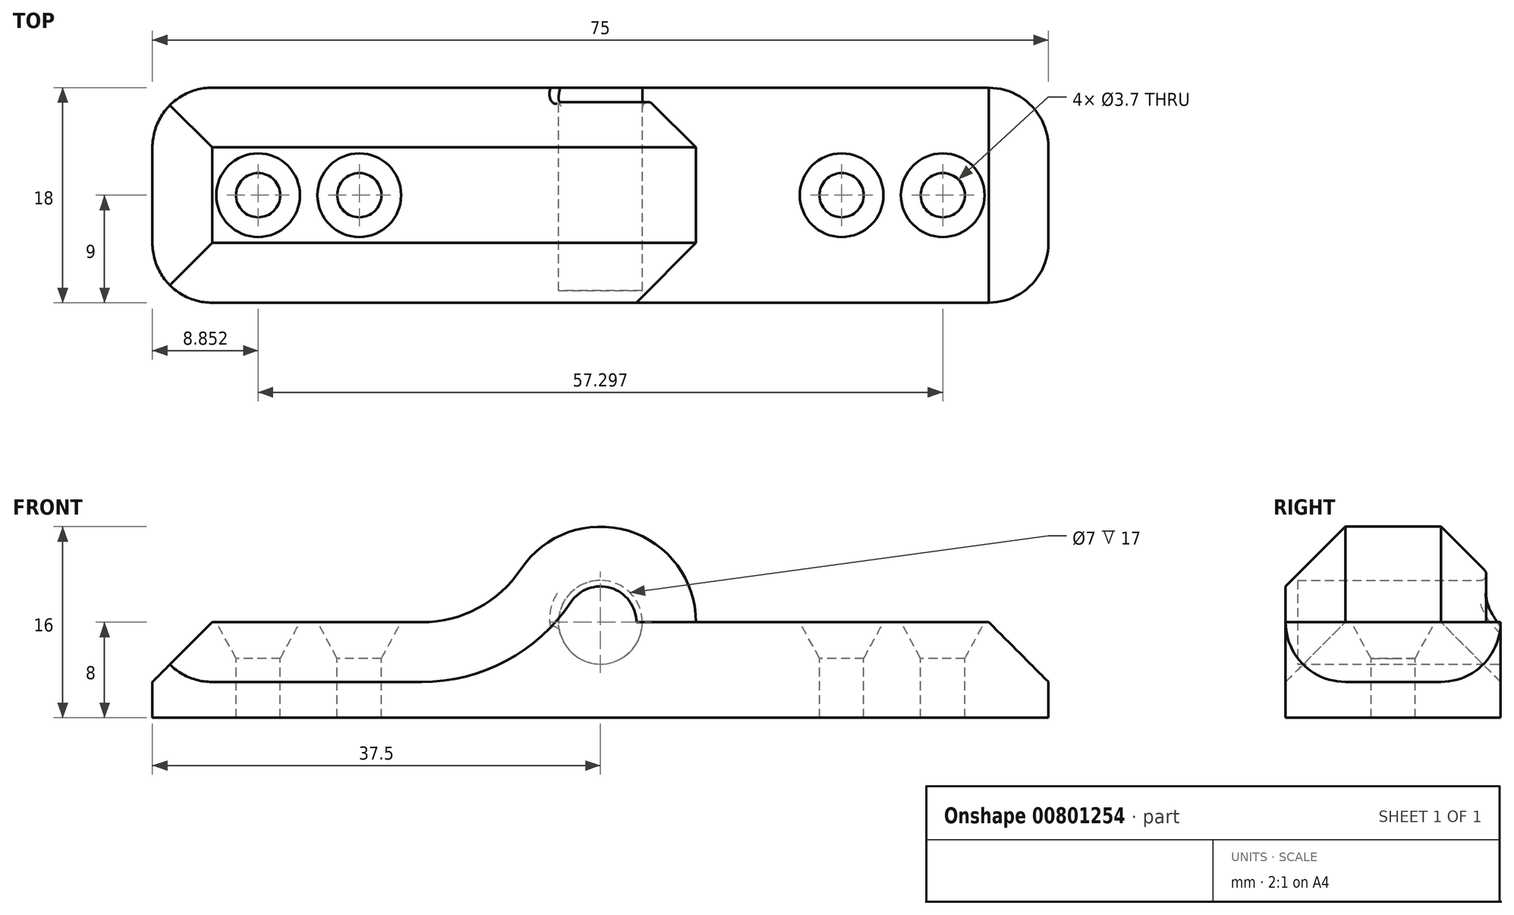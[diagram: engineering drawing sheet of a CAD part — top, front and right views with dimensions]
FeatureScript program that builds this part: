
annotation { "Feature Type Name" : "Feature", "Feature Type Description" : "" }
export const myFeature = defineFeature(function(context is Context, id is Id, definition is map)
    precondition{}
    {
        {
            var Q0;
            Q0=qCreatedBy(makeId("Top.planeOp"),FACE);
            var sketch = newSketch(context, id + "F0", { "sketchPlane" : qUnion([Q0])});
            skLineSegment(sketch, "E0.bottom", {"start": v(37.5, -9) * mm, "end": v(-37.5, -9) * mm});
            skLineSegment(sketch, "E0.top", {"start": v(37.5, 9) * mm, "end": v(-37.5, 9) * mm});
            skLineSegment(sketch, "E0.left", {"start": v(37.5, -9) * mm, "end": v(37.5, 9) * mm});
            skLineSegment(sketch, "E0.right", {"start": v(-37.5, -9) * mm, "end": v(-37.5, 9) * mm});
            skPoint(sketch, "E0.middle", {"position": v(0, 0) * mm});
            skSolve(sketch);
        }
        {
            var Q0;
            Q0 = qSketchRegion(id + "F0", true);
            extrude(context, id + "F1", {"entities" : qUnion([Q0]), "depth" : 8 * mm, "offsetDistance" : 25 * mm});
        }
        {
            var Q0;
            Q0=makeQuery(id+"F1.opExtrude","SWEPT_FACE",FACE,{"disambiguationData":[OSD([sQuery(id+"F0.wireOp",EDGE,"E0.top")])]});
            var sketch = newSketch(context, id + "F2", { "sketchPlane" : qUnion([Q0])});
            skCircle(sketch, "E1", {"center": v(0, 8) * mm, "radius": 8 * mm});
            skCircle(sketch, "E2", {"center": v(0, 8) * mm, "radius": 3.5 * mm});
            skSolve(sketch);
        }
        {
            var Q0;
            {var subQ0=sQuery(id+"F2.wireOp",EDGE,"E1");var subQ1=makeQuery(id+"F1.opExtrude","CAP_EDGE",EDGE,{"disambiguationData":[OSD([sQuery(id+"F0.wireOp",EDGE,"E0.top")])],"isStart":false});var subQ2=makeQuery(id+"F2.imprint","INTERSECT",VERTEX,{"disambiguationData":[OD(0.0)],"derivedFrom":[subQ1,subQ0]});Q0=makeQuery(id+"F2.imprint","IMPRINT",FACE,{"disambiguationData":[TD([[makeQuery(id+"F2.imprint","IMPRINT",EDGE,{"disambiguationData":[TD([[subQ2,1.0]])],"derivedFrom":subQ0}),1.0]])]});}
            var Q1;
            {var subQ0=sQuery(id+"F2.wireOp",EDGE,"E2");var subQ1=makeQuery(id+"F1.opExtrude","CAP_EDGE",EDGE,{"disambiguationData":[OSD([sQuery(id+"F0.wireOp",EDGE,"E0.top")])],"isStart":false});var subQ2=makeQuery(id+"F2.imprint","INTERSECT",VERTEX,{"disambiguationData":[OD(0.0)],"derivedFrom":[subQ1,subQ0]});Q1=makeQuery(id+"F2.imprint","IMPRINT",FACE,{"disambiguationData":[TD([[makeQuery(id+"F2.imprint","IMPRINT",EDGE,{"disambiguationData":[TD([[subQ2,1.0]])],"derivedFrom":subQ0}),1.0]])]});}
            extrude(context, id + "F3", {"entities" : qUnion([Q0, Q1]), "operationType" : NewBodyOperationType.ADD, "depth" : -18 * mm, "offsetDistance" : 25 * mm});
        }
        {
            var Q0;
            {var subQ0=sQuery(id+"F2.wireOp",EDGE,"E2");var subQ1=makeQuery(id+"F1.opExtrude","CAP_EDGE",EDGE,{"disambiguationData":[OSD([sQuery(id+"F0.wireOp",EDGE,"E0.top")])],"isStart":false});var subQ2=makeQuery(id+"F2.imprint","INTERSECT",VERTEX,{"disambiguationData":[OD(0.0)],"derivedFrom":[subQ1,subQ0]});Q0=makeQuery(id+"F2.imprint","IMPRINT",FACE,{"disambiguationData":[TD([[makeQuery(id+"F2.imprint","IMPRINT",EDGE,{"disambiguationData":[TD([[subQ2,-1.0]])],"derivedFrom":subQ0}),1.0]])]});}
            var Q1;
            {var subQ0=sQuery(id+"F2.wireOp",EDGE,"E2");var subQ1=makeQuery(id+"F1.opExtrude","CAP_EDGE",EDGE,{"disambiguationData":[OSD([sQuery(id+"F0.wireOp",EDGE,"E0.top")])],"isStart":false});var subQ2=makeQuery(id+"F2.imprint","INTERSECT",VERTEX,{"disambiguationData":[OD(0.0)],"derivedFrom":[subQ1,subQ0]});Q1=makeQuery(id+"F2.imprint","IMPRINT",FACE,{"disambiguationData":[TD([[makeQuery(id+"F2.imprint","IMPRINT",EDGE,{"disambiguationData":[TD([[subQ2,1.0]])],"derivedFrom":subQ0}),1.0]])]});}
            extrude(context, id + "F4", {"entities" : qUnion([Q0, Q1]), "operationType" : NewBodyOperationType.REMOVE, "oppositeDirection" : true, "depth" : 17 * mm, "offsetDistance" : 25 * mm});
        }
        {
            var Q0;
            {var subQ0=sQuery(id+"F2.wireOp",EDGE,"E1");var subQ1=sQuery(id+"F0.wireOp",EDGE,"E0.top");Q0=makeQuery(id+"F3.opExtrude","SWEPT_EDGE",EDGE,{"disambiguationData":[OSD([subQ1,subQ0]),TDD([makeQuery(id+"F2.imprint","INTERSECT",VERTEX,{"disambiguationData":[OD(1.0)],"derivedFrom":[makeQuery(id+"F1.opExtrude","CAP_EDGE",EDGE,{"disambiguationData":[OSD([subQ1])],"isStart":false}),subQ0]})])]});}
            var Q1;
            {var subQ0=sQuery(id+"F2.wireOp",EDGE,"E1");var subQ1=sQuery(id+"F0.wireOp",EDGE,"E0.top");Q1=makeQuery(id+"F3.opExtrude","SWEPT_EDGE",EDGE,{"disambiguationData":[OSD([subQ1,subQ0]),TDD([makeQuery(id+"F2.imprint","INTERSECT",VERTEX,{"disambiguationData":[OD(0.0)],"derivedFrom":[makeQuery(id+"F1.opExtrude","CAP_EDGE",EDGE,{"disambiguationData":[OSD([subQ1])],"isStart":false}),subQ0]})])]});}
            fillet(context, id + "F5", {"entities" : qUnion([Q0, Q1]), "radius" : 10 * mm, "tangentPropagation" : true, "allowEdgeOverflow" : false});
        }
        {
            var Q0;
            {var subQ0=sQuery(id+"F0.wireOp",EDGE,"E0.right");var subQ2=sQuery(id+"F0.wireOp",EDGE,"E0.top");Q0=makeQuery(id+"F3.boolean.opBoolean","SPLIT",EDGE,{"disambiguationData":[TD([makeQuery(id+"F1.opExtrude","SWEPT_FACE",FACE,{"disambiguationData":[OSD([subQ0])]})])],"derivedFrom":makeQuery(id+"F1.opExtrude","CAP_EDGE",EDGE,{"disambiguationData":[OSD([subQ2])],"isStart":false})});}
            var Q1;
            Q1=makeQuery(id+"F1.opExtrude","CAP_EDGE",EDGE,{"disambiguationData":[OSD([sQuery(id+"F0.wireOp",EDGE,"E0.right")])],"isStart":false});
            var Q2;
            {var subQ1=sQuery(id+"F0.wireOp",EDGE,"E0.right");var subQ3=sQuery(id+"F0.wireOp",EDGE,"E0.bottom");Q2=makeQuery(id+"F3.boolean.opBoolean","SPLIT",EDGE,{"disambiguationData":[TD([makeQuery(id+"F1.opExtrude","SWEPT_FACE",FACE,{"disambiguationData":[OSD([subQ1])]})])],"derivedFrom":makeQuery(id+"F1.opExtrude","CAP_EDGE",EDGE,{"disambiguationData":[OSD([subQ3])],"isStart":false})});}
            var Q3;
            Q3=makeQuery(id+"F1.opExtrude","CAP_EDGE",EDGE,{"disambiguationData":[OSD([sQuery(id+"F0.wireOp",EDGE,"E0.left")])],"isStart":false});
            chamfer(context, id + "F6", {"entities" : qUnion([Q0, Q1, Q2, Q3]), "width" : 5 * mm, "tangentPropagation" : true});
        }
        {
            var Q0;
            {var subQ1=sQuery(id+"F0.wireOp",EDGE,"E0.top");var subQ2=sQuery(id+"F0.wireOp",EDGE,"E0.right");var subQ3=sQuery(id+"F0.wireOp",EDGE,"E0.bottom");Q0=makeQuery(id+"F3.boolean.opBoolean","SPLIT",FACE,{"disambiguationData":[TD([makeQuery(id+"F1.opExtrude","SWEPT_FACE",FACE,{"disambiguationData":[OSD([subQ2])]})])],"derivedFrom":makeQuery(id+"F1.opExtrude","CAP_FACE",FACE,{"disambiguationData":[OSD([subQ3,subQ1,sQuery(id+"F0.wireOp",EDGE,"E0.left"),subQ2])],"isStart":false})});}
            var sketch = newSketch(context, id + "F7", { "sketchPlane" : qUnion([Q0])});
            skPoint(sketch, "E3", {"position": v(-28.65, 0) * mm});
            skPoint(sketch, "E3.positionSnap0", {"position": v(-32.5, 0) * mm});
            skPoint(sketch, "E4", {"position": v(-20.19, 0) * mm});
            skPoint(sketch, "E5.MirrorP", {"position": v(20.19, 0) * mm});
            skPoint(sketch, "E6.MirrorP", {"position": v(28.65, 0) * mm});
            skSolve(sketch);
        }
        {
            var Q0;
            Q0=sQuery(id+"F7.wireOp",VERTEX,"E3");
            var Q1;
            Q1=sQuery(id+"F7.wireOp",VERTEX,"E4");
            var Q2;
            Q2=sQuery(id+"F7.wireOp",VERTEX,"E5.MirrorP");
            var Q3;
            Q3=sQuery(id+"F7.wireOp",VERTEX,"E6.MirrorP");
            var Q4;
            Q4=makeQuery(id+"F1.opExtrude","SWEPT_BODY",BODY,{"disambiguationData":[OSD([sQuery(id+"F0.wireOp",EDGE,"E0.bottom"),sQuery(id+"F0.wireOp",EDGE,"E0.top"),sQuery(id+"F0.wireOp",EDGE,"E0.left"),sQuery(id+"F0.wireOp",EDGE,"E0.right")])]});
            hole(context, id + "F8", {"style" : HoleStyle.C_SINK, "endStyle" : HoleEndStyle.THROUGH, "holeDiameter" : 3.7 * mm, "cSinkDiameter" : 7 * mm, "cSinkAngle" : 57 * degree, "majorDiameter" : 5 * mm, "isTappedThrough" : true, "tappedDepth" : 12 * mm, "tapClearance" : 3, "locations" : qUnion([Q0, Q1, Q2, Q3]), "scope" : qUnion([Q4])});
        }
        {
            var Q0;
            Q0=makeQuery(id+"F1.opExtrude","SWEPT_EDGE",EDGE,{"disambiguationData":[OSD([sQuery(id+"F0.wireOp",EDGE,"E0.bottom"),sQuery(id+"F0.wireOp",EDGE,"E0.right")])]});
            var Q1;
            Q1=makeQuery(id+"F1.opExtrude","SWEPT_EDGE",EDGE,{"disambiguationData":[OSD([sQuery(id+"F0.wireOp",EDGE,"E0.top"),sQuery(id+"F0.wireOp",EDGE,"E0.right")])]});
            var Q2;
            Q2=makeQuery(id+"F1.opExtrude","SWEPT_EDGE",EDGE,{"disambiguationData":[OSD([sQuery(id+"F0.wireOp",EDGE,"E0.top"),sQuery(id+"F0.wireOp",EDGE,"E0.left")])]});
            var Q3;
            Q3=makeQuery(id+"F1.opExtrude","SWEPT_EDGE",EDGE,{"disambiguationData":[OSD([sQuery(id+"F0.wireOp",EDGE,"E0.bottom"),sQuery(id+"F0.wireOp",EDGE,"E0.left")])]});
            fillet(context, id + "F9", {"entities" : qUnion([Q0, Q1, Q2, Q3]), "radius" : 5 * mm, "tangentPropagation" : true, "allowEdgeOverflow" : false});
        }
        {
            var Q0;
            Q0=makeQuery(id+"F6.opChamfer","BLEND_EDGE",EDGE,{"blendedFrom":[makeQuery(id+"F3.opExtrude","CAP_EDGE",EDGE,{"disambiguationData":[OSD([sQuery(id+"F2.wireOp",EDGE,"E1")])],"isStart":true}),makeQuery(id+"F4.boolean.opBoolean","COPY",FACE,{"derivedFrom":makeQuery(id+"F4.opExtrude","SWEPT_FACE",FACE,{"disambiguationData":[OSD([sQuery(id+"F2.wireOp",EDGE,"E2")])]})})],"blendedInto":[makeQuery(id+"F4.boolean.opBoolean","COPY",FACE,{"derivedFrom":makeQuery(id+"F4.opExtrude","SWEPT_FACE",FACE,{"disambiguationData":[OSD([sQuery(id+"F2.wireOp",EDGE,"E2")])]})})]});
            var Q1;
            Q1=makeQuery(id+"F4.boolean.opBoolean","COPY",EDGE,{"derivedFrom":makeQuery(id+"F4.opExtrude","CAP_EDGE",EDGE,{"disambiguationData":[OSD([sQuery(id+"F2.wireOp",EDGE,"E2")])],"isStart":true})});
            fillet(context, id + "F10", {"entities" : qUnion([Q0, Q1]), "radius" : 0.5 * mm, "tangentPropagation" : true, "allowEdgeOverflow" : false});
        }
    });
